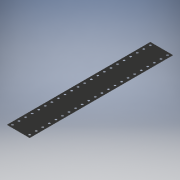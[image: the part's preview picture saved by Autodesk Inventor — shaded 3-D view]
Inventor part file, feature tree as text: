
AUTODESK INVENTOR PART (.ipt)
format: ipt  version: 2019 (Build 230136000, 136)  size: 162,304 bytes
history: native  units: mm
features: extrude x1, other x1
ambient origin geometry x8: Origin, YZ Plane, XZ Plane, XY Plane, X Axis, Y Axis, Z Axis, Center Point
bodies: Body1 (feature_tree)
feature tree (2):
  extrude  "Foam Body"  Depth=1199.0mm
  other  "Foam Scheme"
